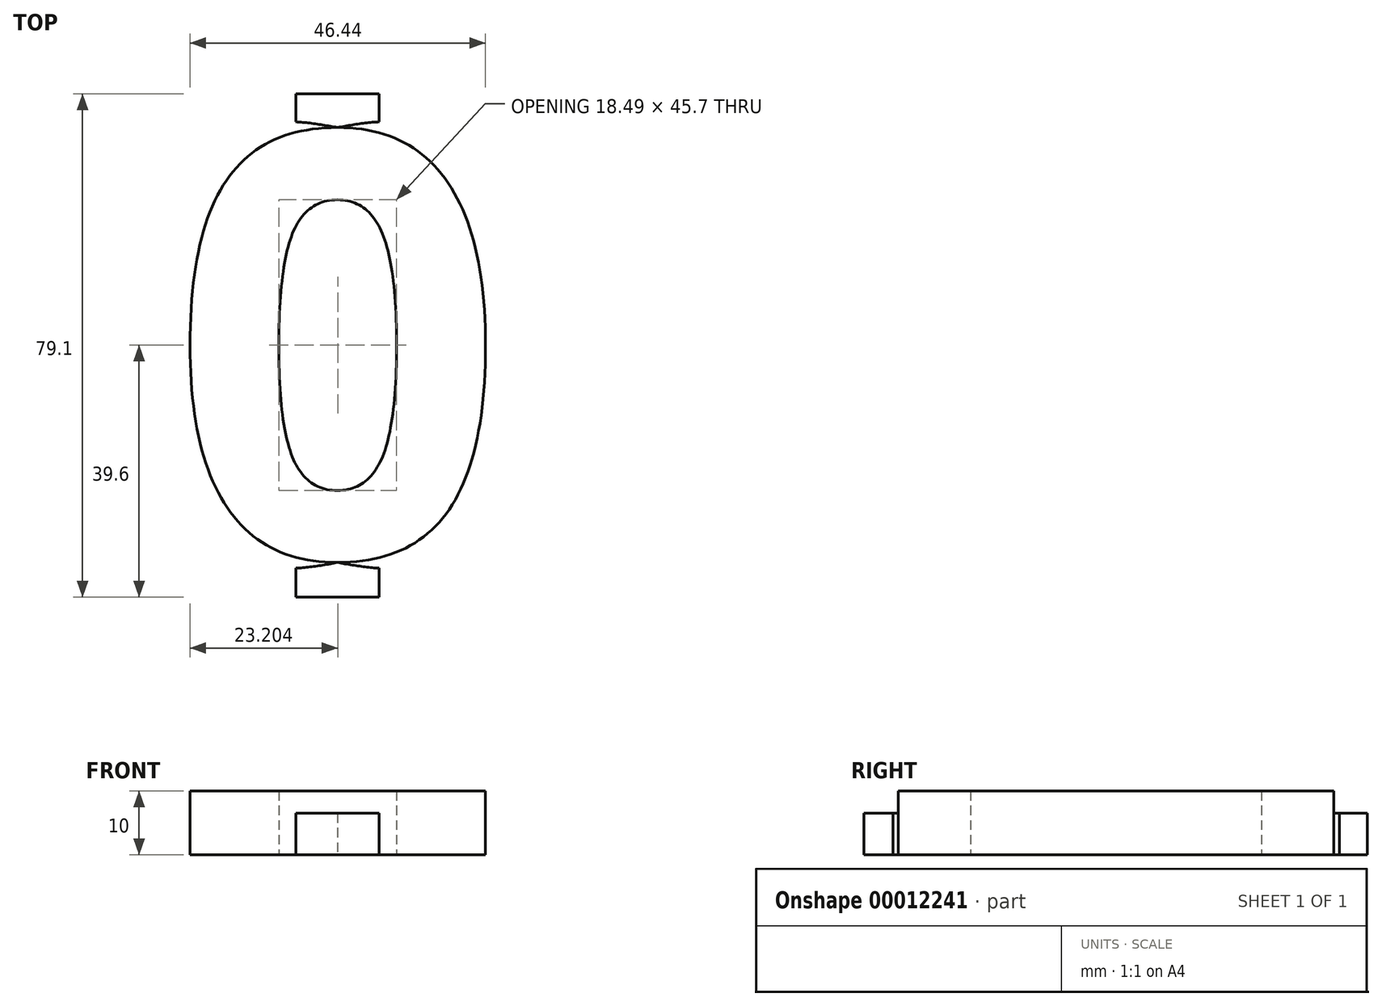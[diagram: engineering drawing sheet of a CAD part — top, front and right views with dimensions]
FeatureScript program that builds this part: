
annotation { "Feature Type Name" : "Feature", "Feature Type Description" : "" }
export const myFeature = defineFeature(function(context is Context, id is Id, definition is map)
    precondition{}
    {
        {
            var Q0;
            Q0=qCreatedBy(makeId("Top.planeOp"),FACE);
            var sketch = newSketch(context, id + "F0", { "sketchPlane" : qUnion([Q0])});
            skText(sketch, "E0", { "text": "0\n", "fontName": "OpenSans-Bold.ttf"});
            const initialGuessF0  = {"E0": [-0.0498, 0, 1, 0, 0.067]};
            skSetInitialGuess(sketch, initialGuessF0);
            skSolve(sketch);
        }
        {
            var Q0;
            Q0=makeQuery(id+"F0.imprint","IMPRINT",FACE,{"disambiguationData":[TD([[makeQuery(id+"F0.imprint","IMPRINT",EDGE,{"derivedFrom":sQuery(id+"F0.wireOp",EDGE,"E0.sketch_text.stroke-0")}),-1.0]])]});
            extrude(context, id + "F1", {"entities" : qUnion([Q0]), "depth" : 10 * mm});
        }
        {
            var Q0;
            Q0=qCreatedBy(makeId("Top.planeOp"),FACE);
            var sketch = newSketch(context, id + "F2", { "sketchPlane" : qUnion([Q0])});
            skFitSpline(sketch, "E1.0.0", {"points": [v(-5.7, 7.45) * mm, v(0, 15.82) * mm, v(0, 33.2) * mm]});
            skFitSpline(sketch, "E1.0.1", {"points": [v(0, 33.2) * mm, v(0, 50.03) * mm, v(-5.88, 58.76) * mm]});
            skFitSpline(sketch, "E1.0.2", {"points": [v(-5.88, 58.76) * mm, v(-11.76, 67.48) * mm, v(-23.26, 67.48) * mm]});
            skFitSpline(sketch, "E1.0.3", {"points": [v(-23.26, 67.48) * mm, v(-35.07, 67.48) * mm, v(-40.76, 59.14) * mm]});
            skFitSpline(sketch, "E1.0.4", {"points": [v(-40.76, 59.14) * mm, v(-46.44, 50.8) * mm, v(-46.44, 33.2) * mm]});
            skFitSpline(sketch, "E1.0.5", {"points": [v(-46.44, 33.2) * mm, v(-46.44, 16.36) * mm, v(-40.6, 7.72) * mm]});
            skFitSpline(sketch, "E1.0.6", {"points": [v(-40.6, 7.72) * mm, v(-34.76, -0.92) * mm, v(-23.26, -0.92) * mm]});
            skFitSpline(sketch, "E1.0.7", {"points": [v(-23.26, -0.92) * mm, v(-11.4, -0.92) * mm, v(-5.7, 7.45) * mm]});
            skLineSegment(sketch, "E2", {"start": v(-46.44, 33.2) * mm, "end": v(-46.44, 67.48) * mm, "construction": true});
            skLineSegment(sketch, "E3", {"start": v(-46.44, 67.48) * mm, "end": v(-23.26, 67.48) * mm, "construction": true});
            skLineSegment(sketch, "E4", {"start": v(-23.26, 67.48) * mm, "end": v(0, 67.48) * mm, "construction": true});
            skLineSegment(sketch, "E5", {"start": v(0, 67.48) * mm, "end": v(0, 33.2) * mm, "construction": true});
            skLineSegment(sketch, "E6", {"start": v(0, 0) * mm, "end": v(0, -0.92) * mm, "construction": true});
            skLineSegment(sketch, "E7", {"start": v(0, -0.92) * mm, "end": v(-23.26, -0.92) * mm, "construction": true});
            skLineSegment(sketch, "E8", {"start": v(-23.26, -0.92) * mm, "end": v(-46.44, -0.92) * mm, "construction": true});
            skLineSegment(sketch, "E9", {"start": v(-46.44, -0.92) * mm, "end": v(-46.44, 33.2) * mm, "construction": true});
            skLineSegment(sketch, "E10", {"start": v(-46.44, 0) * mm, "end": v(0, 0) * mm, "construction": true});
            skLineSegment(sketch, "E11", {"start": v(-46.44, 66.36) * mm, "end": v(0, 66.36) * mm, "construction": true});
            skLineSegment(sketch, "E12.bottom", {"start": v(-23.26, 66.36) * mm, "end": v(-29.8, 66.36) * mm});
            skLineSegment(sketch, "E12.top", {"start": v(-23.26, 72.76) * mm, "end": v(-29.8, 72.76) * mm});
            skLineSegment(sketch, "E12.left", {"start": v(-23.26, 66.36) * mm, "end": v(-23.26, 72.76) * mm});
            skLineSegment(sketch, "E12.right", {"start": v(-29.8, 66.36) * mm, "end": v(-29.8, 72.76) * mm});
            skLineSegment(sketch, "E13.bottom", {"start": v(-23.26, 66.36) * mm, "end": v(-16.72, 66.36) * mm});
            skLineSegment(sketch, "E13.top", {"start": v(-23.26, 72.76) * mm, "end": v(-16.72, 72.76) * mm});
            skLineSegment(sketch, "E13.right", {"start": v(-16.72, 66.36) * mm, "end": v(-16.72, 72.76) * mm});
            skLineSegment(sketch, "E14", {"start": v(-46.44, 33.2) * mm, "end": v(0, 33.2) * mm, "construction": true});
            skLineSegment(sketch, "E15", {"start": v(-46.44, 33.2) * mm, "end": v(0, 33.2) * mm});
            skLineSegment(sketch, "E16.0.MirrorCS", {"start": v(-23.26, -6.34) * mm, "end": v(-16.72, -6.34) * mm});
            skLineSegment(sketch, "E16.1.MirrorCS", {"start": v(-23.26, -6.34) * mm, "end": v(-29.8, -6.34) * mm});
            skLineSegment(sketch, "E16.2.MirrorCS", {"start": v(-16.72, 0.06) * mm, "end": v(-16.72, -6.34) * mm});
            skLineSegment(sketch, "E16.3.MirrorCS", {"start": v(-23.26, 0.06) * mm, "end": v(-16.72, 0.06) * mm});
            skLineSegment(sketch, "E16.4.MirrorCS", {"start": v(-23.26, 0.06) * mm, "end": v(-23.26, -6.34) * mm});
            skLineSegment(sketch, "E16.5.MirrorCS", {"start": v(-23.26, 0.06) * mm, "end": v(-29.8, 0.06) * mm});
            skLineSegment(sketch, "E16.6.MirrorCS", {"start": v(-29.8, 0.06) * mm, "end": v(-29.8, -6.34) * mm});
            skLineSegment(sketch, "E16.7.MirrorCS", {"start": v(-23.26, 0.06) * mm, "end": v(-23.26, -6.34) * mm});
            skSolve(sketch);
        }
        {
            var Q0;
            {var subQ1=sQuery(id+"F2.wireOp",EDGE,"E12.top");Q0=makeQuery(id+"F2.imprint","IMPRINT",FACE,{"disambiguationData":[TD([[makeQuery(id+"F2.imprint","IMPRINT",EDGE,{"derivedFrom":subQ1}),1.0]])]});}
            var Q1;
            {var subQ3=sQuery(id+"F2.wireOp",EDGE,"E13.top");Q1=makeQuery(id+"F2.imprint","IMPRINT",FACE,{"disambiguationData":[TD([[makeQuery(id+"F2.imprint","IMPRINT",EDGE,{"derivedFrom":subQ3}),-1.0]])]});}
            extrude(context, id + "F3", {"entities" : qUnion([Q0, Q1]), "operationType" : NewBodyOperationType.ADD, "depth" : 6.5 * mm});
        }
        {
            var Q0;
            {var subQ3=sQuery(id+"F2.wireOp",EDGE,"E16.1.MirrorCS");Q0=makeQuery(id+"F2.imprint","IMPRINT",FACE,{"disambiguationData":[TD([[makeQuery(id+"F2.imprint","IMPRINT",EDGE,{"derivedFrom":subQ3}),-1.0]])]});}
            var Q1;
            {var subQ1=sQuery(id+"F2.wireOp",EDGE,"E16.0.MirrorCS");Q1=makeQuery(id+"F2.imprint","IMPRINT",FACE,{"disambiguationData":[TD([[makeQuery(id+"F2.imprint","IMPRINT",EDGE,{"derivedFrom":subQ1}),1.0]])]});}
            extrude(context, id + "F4", {"entities" : qUnion([Q0, Q1]), "operationType" : NewBodyOperationType.ADD, "depth" : 6.5 * mm});
        }
    });
